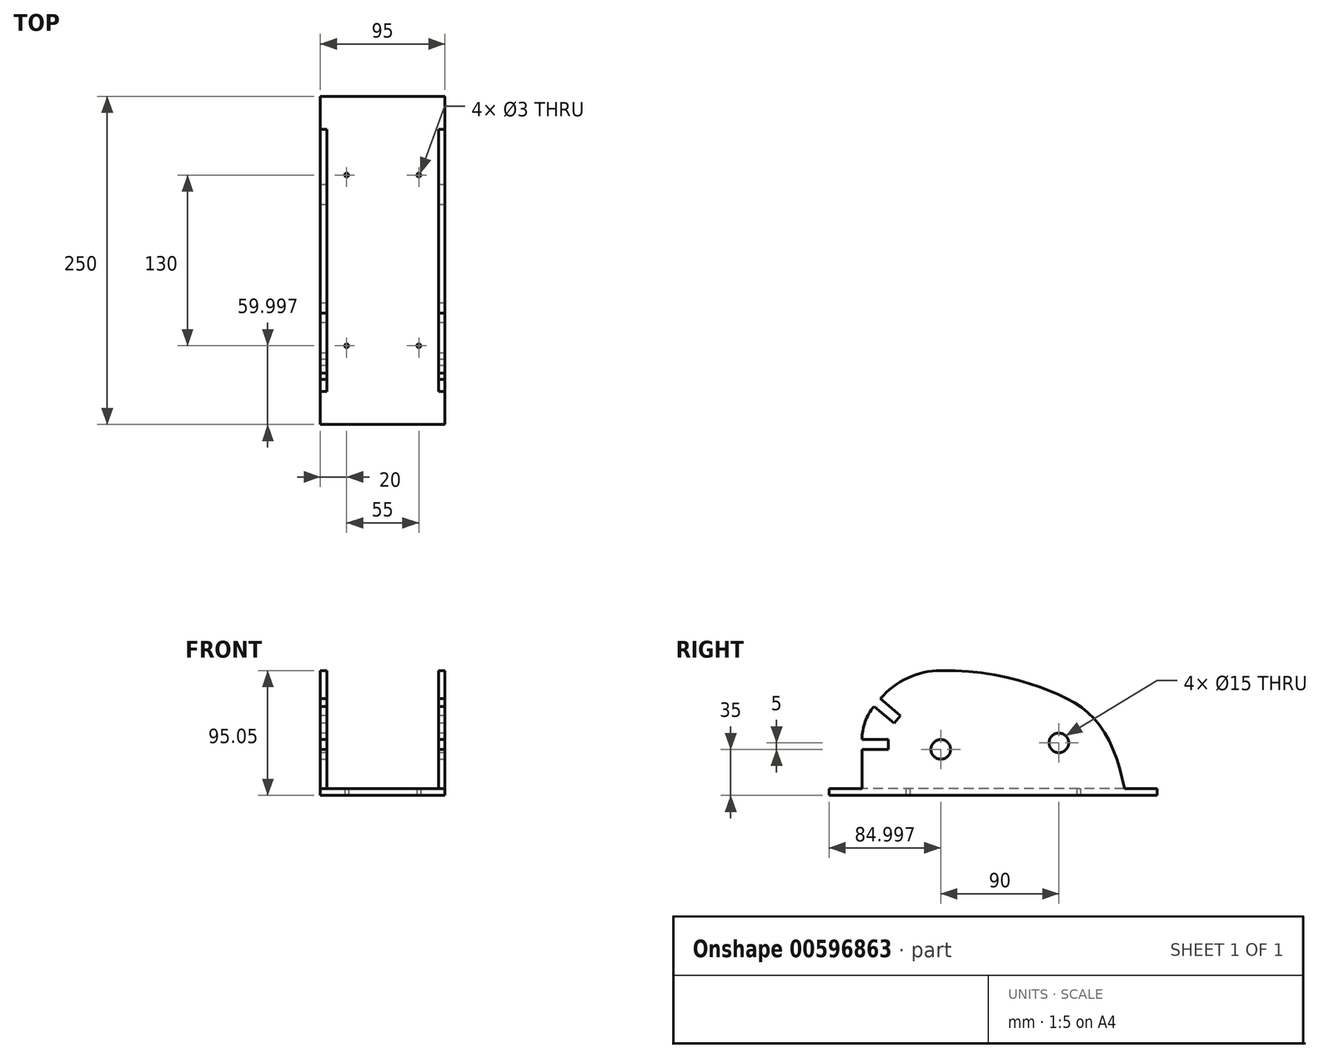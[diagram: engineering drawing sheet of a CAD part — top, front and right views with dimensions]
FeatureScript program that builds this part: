
annotation { "Feature Type Name" : "Feature", "Feature Type Description" : "" }
export const myFeature = defineFeature(function(context is Context, id is Id, definition is map)
    precondition{}
    {
        {
            var Q0;
            Q0=qCreatedBy(makeId("Right.planeOp"),FACE);
            var sketch = newSketch(context, id + "F0", { "sketchPlane" : qUnion([Q0])});
            skLineSegment(sketch, "E0.bottom", {"start": v(-88, 0) * mm, "end": v(162, 0) * mm});
            skLineSegment(sketch, "E0.top", {"start": v(-88, 5) * mm, "end": v(162, 5) * mm});
            skLineSegment(sketch, "E0.left", {"start": v(-88, 0) * mm, "end": v(-88, 5) * mm});
            skLineSegment(sketch, "E0.right", {"start": v(162, 0) * mm, "end": v(162, 5) * mm});
            skLineSegment(sketch, "E1", {"start": v(-88, 5) * mm, "end": v(-63, 5) * mm});
            skLineSegment(sketch, "E2", {"start": v(-63, 5) * mm, "end": v(-3, 5) * mm});
            skLineSegment(sketch, "E3.top", {"start": v(-3, 5) * mm, "end": v(-63, 5) * mm});
            skLineSegment(sketch, "E3.right", {"start": v(-63, 35) * mm, "end": v(-63, 5) * mm});
            skLineSegment(sketch, "E4.bottom", {"start": v(-63, 35) * mm, "end": v(-43, 35) * mm});
            skLineSegment(sketch, "E4.top", {"start": v(-63, 42.5) * mm, "end": v(-43, 42.5) * mm});
            skLineSegment(sketch, "E4.right", {"start": v(-43, 35) * mm, "end": v(-43, 42.5) * mm});
            skCircle(sketch, "E5", {"center": v(-3, 35) * mm, "radius": 7.5 * mm});
            skLineSegment(sketch, "E6", {"start": v(-53.78, 67.82) * mm, "end": v(-38.46, 54.97) * mm});
            skLineSegment(sketch, "E7", {"start": v(-38.46, 54.97) * mm, "end": v(-33.63, 60.71) * mm});
            skLineSegment(sketch, "E8", {"start": v(162, 5) * mm, "end": v(137, 5) * mm});
            skLineSegment(sketch, "E9", {"start": v(137, 5) * mm, "end": v(87, 5) * mm});
            skLineSegment(sketch, "E10", {"start": v(87, 5) * mm, "end": v(87, 40) * mm});
            skCircle(sketch, "E11", {"center": v(87, 40) * mm, "radius": 7.5 * mm});
            skArc(sketch, "E12", {"start": v(-3, 95) * mm, "mid": v(-28.35, 89.38) * mm, "end": v(-48.96, 73.57) * mm});
            skArc(sketch, "E13", {"start": v(-53.78, 67.82) * mm, "mid": v(-60.62, 55.97) * mm, "end": v(-63, 42.5) * mm});
            skLineSegment(sketch, "E14", {"start": v(-3, 95) * mm, "end": v(-3, 42.5) * mm});
            skLineSegment(sketch, "E15", {"start": v(-3, 5) * mm, "end": v(-3, 27.5) * mm});
            skLineSegment(sketch, "E16", {"start": v(-48.96, 73.57) * mm, "end": v(-33.63, 60.71) * mm});
            skFitSpline(sketch, "E17", {"points": [v(-3, 95) * mm, v(80.93, 79.26) * mm, v(116.88, 54.94) * mm, v(137, 5) * mm], "startDerivative": vector(252.83, 5.54) * mm, "endDerivative": vector(35.75, -183.6) * mm});
            skSolve(sketch);
        }
        {
            var Q0;
            Q0 = qSketchRegion(id + "F0", true);
            extrude(context, id + "F1", {"entities" : qUnion([Q0]), "depth" : 95 * mm, "offsetDistance" : 25 * mm});
        }
        {
            var Q0;
            Q0=qCreatedBy(makeId("Front.planeOp"),FACE);
            var sketch = newSketch(context, id + "F2", { "sketchPlane" : qUnion([Q0])});
            skLineSegment(sketch, "E18.top", {"start": v(90, 5) * mm, "end": v(5, 5) * mm});
            skLineSegment(sketch, "E18.left", {"start": v(90, 95) * mm, "end": v(90, 5) * mm});
            skLineSegment(sketch, "E18.right", {"start": v(5, 95) * mm, "end": v(5, 5) * mm});
            skLineSegment(sketch, "E19", {"start": v(5, 5) * mm, "end": v(90, 5) * mm});
            skLineSegment(sketch, "E20.top", {"start": v(90, 99.05) * mm, "end": v(5, 99.05) * mm});
            skLineSegment(sketch, "E20.left", {"start": v(90, 95) * mm, "end": v(90, 99.05) * mm});
            skLineSegment(sketch, "E20.right", {"start": v(5, 95) * mm, "end": v(5, 99.05) * mm});
            skSolve(sketch);
        }
        {
            var Q0;
            Q0 = qSketchRegion(id + "F2", true);
            extrude(context, id + "F3", {"entities" : qUnion([Q0]), "operationType" : NewBodyOperationType.REMOVE, "oppositeDirection" : true, "depth" : 150 * mm, "offsetDistance" : 25 * mm, "hasSecondDirection" : true, "secondDirectionOppositeDirection" : false, "secondDirectionDepth" : 150 * mm});
        }
        {
            var Q0;
            Q0=makeQuery(id+"F1.opExtrude","SWEPT_FACE",FACE,{"disambiguationData":[OSD([sQuery(id+"F0.wireOp",EDGE,"E0.bottom")])]});
            var sketch = newSketch(context, id + "F4", { "sketchPlane" : qUnion([Q0])});
            skLineSegment(sketch, "E21.bottom", {"start": v(20, 28) * mm, "end": v(75, 28) * mm});
            skLineSegment(sketch, "E21.top", {"start": v(20, -102) * mm, "end": v(75, -102) * mm});
            skLineSegment(sketch, "E21.left", {"start": v(20, 28) * mm, "end": v(20, -102) * mm});
            skLineSegment(sketch, "E21.right", {"start": v(75, 28) * mm, "end": v(75, -102) * mm});
            skCircle(sketch, "E22", {"center": v(20, 28) * mm, "radius": 1.5 * mm});
            skCircle(sketch, "E23", {"center": v(75, 28) * mm, "radius": 1.5 * mm});
            skCircle(sketch, "E24", {"center": v(20, -102) * mm, "radius": 1.5 * mm});
            skCircle(sketch, "E25", {"center": v(75, -102) * mm, "radius": 1.5 * mm});
            skSolve(sketch);
        }
        {
            var Q0;
            {var subQ0=sQuery(id+"F4.wireOp",EDGE,"E21.left");var subQ1=sQuery(id+"F4.wireOp",EDGE,"E21.bottom");var subQ2=makeQuery(id+"F4.imprint","INTERSECT",VERTEX,{"derivedFrom":[subQ1,subQ0]});Q0=makeQuery(id+"F4.imprint","IMPRINT",FACE,{"disambiguationData":[TD([[makeQuery(id+"F4.imprint","IMPRINT",EDGE,{"disambiguationData":[TD([[subQ2,-1.0]])],"derivedFrom":subQ1}),1.0]])]});}
            var Q1;
            {var subQ0=sQuery(id+"F4.wireOp",EDGE,"E21.left");var subQ1=sQuery(id+"F4.wireOp",EDGE,"E21.bottom");var subQ2=makeQuery(id+"F4.imprint","INTERSECT",VERTEX,{"derivedFrom":[subQ1,subQ0]});Q1=makeQuery(id+"F4.imprint","IMPRINT",FACE,{"disambiguationData":[TD([[makeQuery(id+"F4.imprint","IMPRINT",EDGE,{"disambiguationData":[TD([[subQ2,-1.0]])],"derivedFrom":subQ1}),-1.0]])]});}
            var Q2;
            {var subQ0=sQuery(id+"F4.wireOp",EDGE,"E21.right");var subQ1=sQuery(id+"F4.wireOp",EDGE,"E21.bottom");var subQ2=makeQuery(id+"F4.imprint","INTERSECT",VERTEX,{"derivedFrom":[subQ1,subQ0]});Q2=makeQuery(id+"F4.imprint","IMPRINT",FACE,{"disambiguationData":[TD([[makeQuery(id+"F4.imprint","IMPRINT",EDGE,{"disambiguationData":[TD([[subQ2,1.0]])],"derivedFrom":subQ1}),-1.0]])]});}
            var Q3;
            {var subQ0=sQuery(id+"F4.wireOp",EDGE,"E21.right");var subQ1=sQuery(id+"F4.wireOp",EDGE,"E21.bottom");var subQ2=makeQuery(id+"F4.imprint","INTERSECT",VERTEX,{"derivedFrom":[subQ1,subQ0]});Q3=makeQuery(id+"F4.imprint","IMPRINT",FACE,{"disambiguationData":[TD([[makeQuery(id+"F4.imprint","IMPRINT",EDGE,{"disambiguationData":[TD([[subQ2,1.0]])],"derivedFrom":subQ1}),1.0]])]});}
            var Q4;
            {var subQ0=sQuery(id+"F4.wireOp",EDGE,"E21.left");var subQ1=sQuery(id+"F4.wireOp",EDGE,"E21.top");var subQ2=makeQuery(id+"F4.imprint","INTERSECT",VERTEX,{"derivedFrom":[subQ1,subQ0]});Q4=makeQuery(id+"F4.imprint","IMPRINT",FACE,{"disambiguationData":[TD([[makeQuery(id+"F4.imprint","IMPRINT",EDGE,{"disambiguationData":[TD([[subQ2,-1.0]])],"derivedFrom":subQ1}),1.0]])]});}
            var Q5;
            {var subQ0=sQuery(id+"F4.wireOp",EDGE,"E21.left");var subQ1=sQuery(id+"F4.wireOp",EDGE,"E21.top");var subQ2=makeQuery(id+"F4.imprint","INTERSECT",VERTEX,{"derivedFrom":[subQ1,subQ0]});Q5=makeQuery(id+"F4.imprint","IMPRINT",FACE,{"disambiguationData":[TD([[makeQuery(id+"F4.imprint","IMPRINT",EDGE,{"disambiguationData":[TD([[subQ2,-1.0]])],"derivedFrom":subQ1}),-1.0]])]});}
            var Q6;
            {var subQ0=sQuery(id+"F4.wireOp",EDGE,"E21.right");var subQ1=sQuery(id+"F4.wireOp",EDGE,"E21.top");var subQ2=makeQuery(id+"F4.imprint","INTERSECT",VERTEX,{"derivedFrom":[subQ1,subQ0]});Q6=makeQuery(id+"F4.imprint","IMPRINT",FACE,{"disambiguationData":[TD([[makeQuery(id+"F4.imprint","IMPRINT",EDGE,{"disambiguationData":[TD([[subQ2,1.0]])],"derivedFrom":subQ1}),1.0]])]});}
            var Q7;
            {var subQ0=sQuery(id+"F4.wireOp",EDGE,"E21.right");var subQ1=sQuery(id+"F4.wireOp",EDGE,"E21.top");var subQ2=makeQuery(id+"F4.imprint","INTERSECT",VERTEX,{"derivedFrom":[subQ1,subQ0]});Q7=makeQuery(id+"F4.imprint","IMPRINT",FACE,{"disambiguationData":[TD([[makeQuery(id+"F4.imprint","IMPRINT",EDGE,{"disambiguationData":[TD([[subQ2,1.0]])],"derivedFrom":subQ1}),-1.0]])]});}
            extrude(context, id + "F5", {"entities" : qUnion([Q0, Q1, Q2, Q3, Q4, Q5, Q6, Q7]), "operationType" : NewBodyOperationType.REMOVE, "oppositeDirection" : true, "depth" : 25 * mm, "offsetDistance" : 25 * mm});
        }
    });
